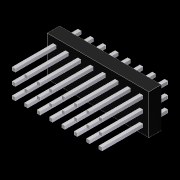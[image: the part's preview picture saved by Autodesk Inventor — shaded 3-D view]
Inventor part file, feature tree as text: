
AUTODESK INVENTOR PART (.ipt)
format: ipt  version: 2012 (Build 160160000, 160)  size: 214,528 bytes
history: native  units: in
note: dims shown in document units (in); Inventor stores cm internally (conversion verified against a paired STEP export)
features: extrude x3, sketch x1, pattern_linear x1
ambient origin geometry x8: Origin, YZ Plane, XZ Plane, XY Plane, X Axis, Y Axis, Z Axis, Center Point
bodies: Solid1 (feature_tree)
feature tree (5):
  sketch  "Sketch1"  dims[d0=0.1in d1=0.0in d2=0.33in d3=0.0in d4=0.2in d5=0.0in d6=1.1811in d8=0.1in d9=3.1496in d11=0.1in]
  extrude  "Extrusion1"  Depth=0.33in TaperAngle=0.0deg
  extrude  "Extrusion2"  Depth=0.2in TaperAngle=0.0deg
  extrude  "Extrusion3"  Depth=1.1811in
  pattern_linear  "Rectangular Pattern1"  Count1=8 Spacing1=0.1in
